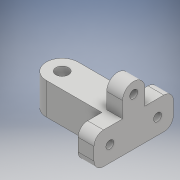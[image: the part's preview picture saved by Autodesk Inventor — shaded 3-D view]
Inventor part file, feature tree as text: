
AUTODESK INVENTOR PART (.ipt)
format: ipt  version: 2017 (Build 210142000, 142)  size: 151,552 bytes
history: native  units: mm
features: extrude x3, sketch x3, fillet x1
ambient origin geometry x8: Origin, YZ Plane, XZ Plane, XY Plane, X Axis, Y Axis, Z Axis, Center Point
bodies: Solid1 (feature_tree)
feature tree (7):
  extrude  "Extrusion1"  Depth=35.0mm
  extrude  "Extrusion2"  Depth=10.0mm
  fillet  "Fillet1"  Radius=10.0mm
  extrude  "Extrusion3"  Depth=10.0mm
  sketch  "Sketch1"  dims[d0=8.0mm d1=35.0mm]
  sketch  "Sketch2"  dims[d2=50.0mm d3=10.0mm d4=10.0mm]
  sketch  "Sketch3"  dims[d5=20.0mm d6=0.0mm d7=5.0mm d8=10.0mm d9=20.0mm d10=0.0mm d11=6.0mm d12=5.0mm d13=7.0mm d14=10.0mm d15=10.0mm d16=0.0mm]
